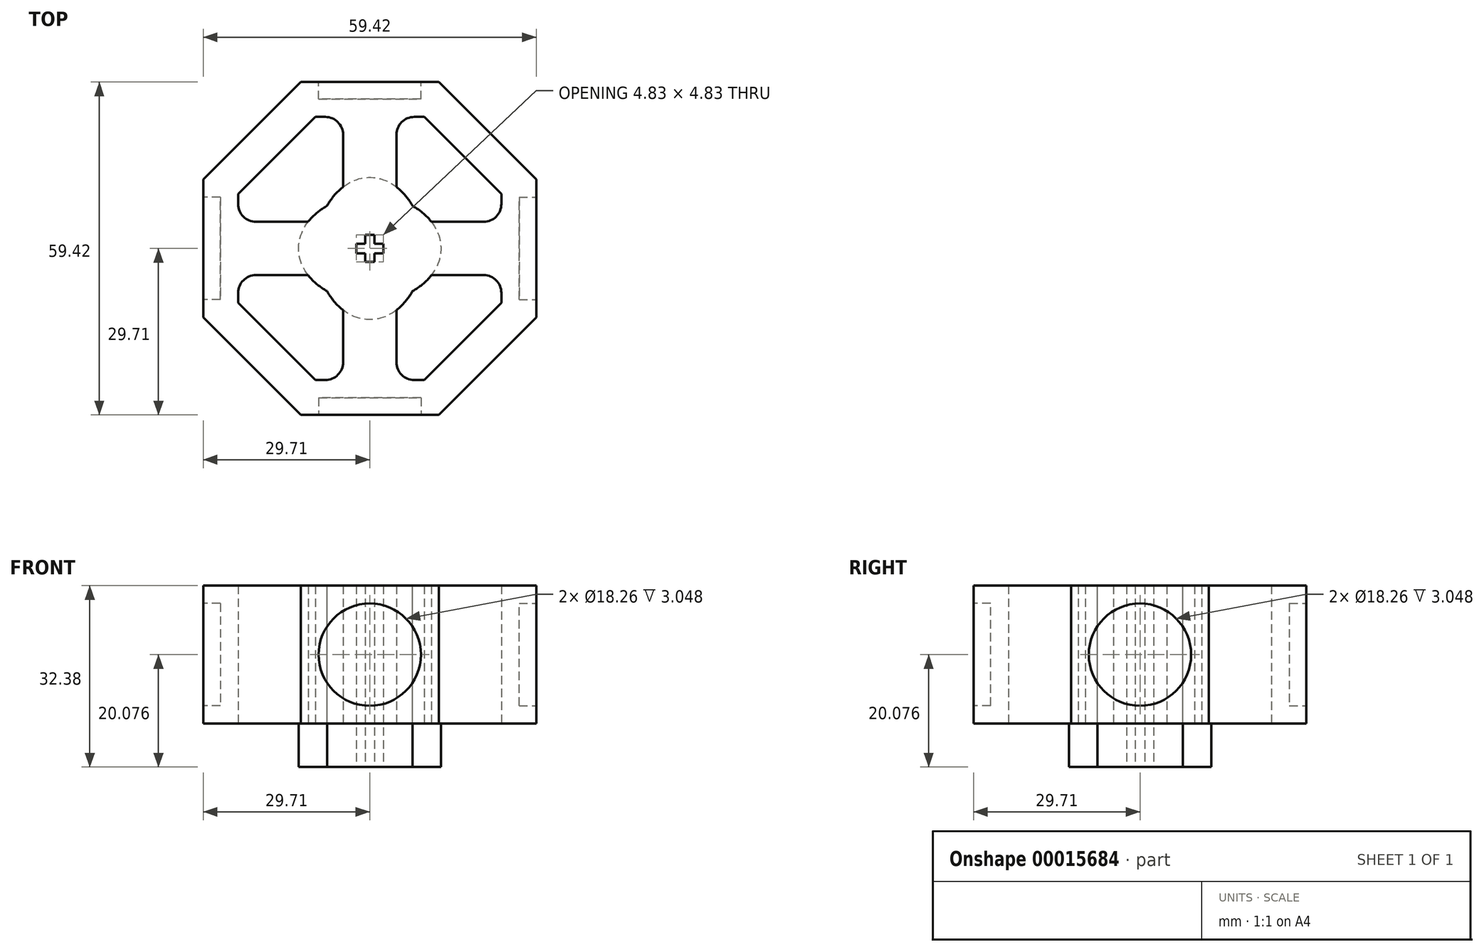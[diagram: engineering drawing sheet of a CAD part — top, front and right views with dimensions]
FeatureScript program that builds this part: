
annotation { "Feature Type Name" : "Feature", "Feature Type Description" : "" }
export const myFeature = defineFeature(function(context is Context, id is Id, definition is map)
    precondition{}
    {
        {
            var Q0;
            Q0=qCreatedBy(makeId("Top.planeOp"),FACE);
            var sketch = newSketch(context, id + "F0", { "sketchPlane" : qUnion([Q0])});
            skCircle(sketch, "E0.cCircle", {"center": v(0, 0) * mm, "radius": 29.71 * mm, "construction": true});
            skLineSegment(sketch, "E0.0", {"start": v(-12.3, 29.71) * mm, "end": v(12.3, 29.71) * mm});
            skLineSegment(sketch, "E0.1", {"start": v(12.3, 29.71) * mm, "end": v(29.71, 12.3) * mm});
            skLineSegment(sketch, "E0.2", {"start": v(29.71, 12.3) * mm, "end": v(29.71, -12.3) * mm});
            skLineSegment(sketch, "E0.3", {"start": v(29.71, -12.3) * mm, "end": v(12.3, -29.71) * mm});
            skLineSegment(sketch, "E0.4", {"start": v(12.3, -29.71) * mm, "end": v(-12.3, -29.71) * mm});
            skLineSegment(sketch, "E0.5", {"start": v(-12.3, -29.71) * mm, "end": v(-29.71, -12.3) * mm});
            skLineSegment(sketch, "E0.6", {"start": v(-29.71, -12.3) * mm, "end": v(-29.71, 12.3) * mm});
            skLineSegment(sketch, "E0.7", {"start": v(-29.71, 12.3) * mm, "end": v(-12.3, 29.71) * mm});
            skPoint(sketch, "E0.0.midPoint", {"position": v(0, 29.71) * mm});
            skLineSegment(sketch, "E1.rect.bottom", {"start": v(0.84, -2.41) * mm, "end": v(-0.84, -2.41) * mm});
            skLineSegment(sketch, "E1.rect.top", {"start": v(0.84, 2.41) * mm, "end": v(-0.84, 2.41) * mm});
            skLineSegment(sketch, "E1.rect.left", {"start": v(0.84, -2.41) * mm, "end": v(0.84, 2.41) * mm});
            skLineSegment(sketch, "E1.rect.right", {"start": v(-0.84, -2.41) * mm, "end": v(-0.84, 2.41) * mm});
            skLineSegment(sketch, "E2.rect.bottom", {"start": v(2.41, -0.84) * mm, "end": v(-2.41, -0.84) * mm});
            skLineSegment(sketch, "E2.rect.top", {"start": v(2.41, 0.84) * mm, "end": v(-2.41, 0.84) * mm});
            skLineSegment(sketch, "E2.rect.left", {"start": v(2.41, -0.84) * mm, "end": v(2.41, 0.84) * mm});
            skLineSegment(sketch, "E2.rect.right", {"start": v(-2.41, -0.84) * mm, "end": v(-2.41, 0.84) * mm});
            skSolve(sketch);
        }
        {
            var Q0;
            Q0 = qSketchRegion(id + "F0", true);
            extrude(context, id + "F1", {"entities" : qUnion([Q0]), "depth" : 24.6 * mm});
        }
        {
            var Q0;
            Q0=makeQuery(id+"F1.opExtrude","SWEPT_FACE",FACE,{"disambiguationData":[OSD([sQuery(id+"F0.wireOp",EDGE,"E0.4")])]});
            var sketch = newSketch(context, id + "F2", { "sketchPlane" : qUnion([Q0])});
            skLineSegment(sketch, "E3", {"start": v(0, 24.61) * mm, "end": v(0, 21.44) * mm});
            skLineSegment(sketch, "E4", {"start": v(0, 21.44) * mm, "end": v(0, 3.18) * mm});
            skLineSegment(sketch, "E5", {"start": v(0, 3.18) * mm, "end": v(0, 0) * mm});
            skCircle(sketch, "E6", {"center": v(0, 12.3) * mm, "radius": 9.13 * mm});
            skSolve(sketch);
        }
        {
            var Q0;
            Q0 = qSketchRegion(id + "F2", true);
            extrude(context, id + "F3", {"entities" : qUnion([Q0]), "operationType" : NewBodyOperationType.REMOVE, "oppositeDirection" : true, "depth" : 3.05 * mm});
        }
        {
            var Q0;
            Q0=makeQuery(id+"F1.opExtrude","SWEPT_FACE",FACE,{"disambiguationData":[OSD([sQuery(id+"F0.wireOp",EDGE,"E0.0")])]});
            var sketch = newSketch(context, id + "F4", { "sketchPlane" : qUnion([Q0])});
            skCircle(sketch, "E7", {"center": v(0, 12.3) * mm, "radius": 9.13 * mm});
            skSolve(sketch);
        }
        {
            var Q0;
            Q0 = qSketchRegion(id + "F4", true);
            extrude(context, id + "F5", {"entities" : qUnion([Q0]), "operationType" : NewBodyOperationType.REMOVE, "oppositeDirection" : true, "depth" : 3.05 * mm});
        }
        {
            var Q0;
            Q0=makeQuery(id+"F1.opExtrude","SWEPT_FACE",FACE,{"disambiguationData":[OSD([sQuery(id+"F0.wireOp",EDGE,"E0.6")])]});
            var sketch = newSketch(context, id + "F6", { "sketchPlane" : qUnion([Q0])});
            skLineSegment(sketch, "E8", {"start": v(0, 0) * mm, "end": v(0, 3.18) * mm});
            skLineSegment(sketch, "E9", {"start": v(0, 3.18) * mm, "end": v(0, 21.44) * mm});
            skLineSegment(sketch, "E10", {"start": v(0, 21.44) * mm, "end": v(0, 24.61) * mm});
            skCircle(sketch, "E11", {"center": v(0, 12.3) * mm, "radius": 9.13 * mm});
            skSolve(sketch);
        }
        {
            var Q0;
            Q0 = qSketchRegion(id + "F6", true);
            extrude(context, id + "F7", {"entities" : qUnion([Q0]), "operationType" : NewBodyOperationType.REMOVE, "oppositeDirection" : true, "depth" : 3.05 * mm});
        }
        {
            var Q0;
            Q0=makeQuery(id+"F1.opExtrude","SWEPT_FACE",FACE,{"disambiguationData":[OSD([sQuery(id+"F0.wireOp",EDGE,"E0.2")])]});
            var sketch = newSketch(context, id + "F8", { "sketchPlane" : qUnion([Q0])});
            skCircle(sketch, "E12", {"center": v(0, 12.3) * mm, "radius": 9.13 * mm});
            skSolve(sketch);
        }
        {
            var Q0;
            Q0 = qSketchRegion(id + "F8", true);
            extrude(context, id + "F9", {"entities" : qUnion([Q0]), "operationType" : NewBodyOperationType.REMOVE, "oppositeDirection" : true, "depth" : 3.05 * mm});
        }
        {
            var Q0;
            Q0=makeQuery(id+"F1.opExtrude","CAP_FACE",FACE,{"disambiguationData":[OSD([sQuery(id+"F0.wireOp",EDGE,"E0.0"),sQuery(id+"F0.wireOp",EDGE,"E0.1"),sQuery(id+"F0.wireOp",EDGE,"E0.2"),sQuery(id+"F0.wireOp",EDGE,"E0.3"),sQuery(id+"F0.wireOp",EDGE,"E0.4"),sQuery(id+"F0.wireOp",EDGE,"E0.5"),sQuery(id+"F0.wireOp",EDGE,"E0.6"),sQuery(id+"F0.wireOp",EDGE,"E0.7"),sQuery(id+"F0.wireOp",EDGE,"E1.rect.bottom"),sQuery(id+"F0.wireOp",EDGE,"E1.rect.top"),sQuery(id+"F0.wireOp",EDGE,"E1.rect.left"),sQuery(id+"F0.wireOp",EDGE,"E1.rect.right"),sQuery(id+"F0.wireOp",EDGE,"E2.rect.bottom"),sQuery(id+"F0.wireOp",EDGE,"E2.rect.top"),sQuery(id+"F0.wireOp",EDGE,"E2.rect.left"),sQuery(id+"F0.wireOp",EDGE,"E2.rect.right")])],"isStart":true});
            var sketch = newSketch(context, id + "F10", { "sketchPlane" : qUnion([Q0])});
            skEllipse(sketch, "E13", {"center": v(0, 0) * mm, "majorRadius": 12.7 * mm, "minorRadius": 9.53 * mm, "majorAxis": v(0, 1)});
            skEllipse(sketch, "E14", {"center": v(0, 0) * mm, "majorRadius": 12.7 * mm, "minorRadius": 9.53 * mm, "majorAxis": v(1, 0)});
            skSolve(sketch);
        }
        {
            var Q0;
            {var subQ0=sQuery(id+"F10.wireOp",EDGE,"E14");var subQ1=sQuery(id+"F10.wireOp",EDGE,"E13");var subQ3=makeQuery(id+"F10.imprint","INTERSECT",VERTEX,{"disambiguationData":[OD(0.0)],"derivedFrom":[subQ1,subQ0]});Q0=makeQuery(id+"F10.imprint","IMPRINT",FACE,{"disambiguationData":[TD([[makeQuery(id+"F10.imprint","IMPRINT",EDGE,{"disambiguationData":[TD([[subQ3,1.0]])],"derivedFrom":subQ1}),-1.0]])]});}
            var Q1;
            {var subQ0=sQuery(id+"F10.wireOp",EDGE,"E14");var subQ1=sQuery(id+"F10.wireOp",EDGE,"E13");var subQ3=makeQuery(id+"F10.imprint","INTERSECT",VERTEX,{"disambiguationData":[OD(0.0)],"derivedFrom":[subQ1,subQ0]});Q1=makeQuery(id+"F10.imprint","IMPRINT",FACE,{"disambiguationData":[TD([[makeQuery(id+"F10.imprint","IMPRINT",EDGE,{"disambiguationData":[TD([[subQ3,-1.0]])],"derivedFrom":subQ1}),1.0]])]});}
            var Q2;
            {var subQ0=sQuery(id+"F10.wireOp",EDGE,"E14");var subQ1=sQuery(id+"F10.wireOp",EDGE,"E13");var subQ3=makeQuery(id+"F10.imprint","INTERSECT",VERTEX,{"disambiguationData":[OD(2.0)],"derivedFrom":[subQ1,subQ0]});Q2=makeQuery(id+"F10.imprint","IMPRINT",FACE,{"disambiguationData":[TD([[makeQuery(id+"F10.imprint","IMPRINT",EDGE,{"disambiguationData":[TD([[subQ3,-1.0]])],"derivedFrom":subQ1}),-1.0]])]});}
            var Q3;
            {var subQ0=sQuery(id+"F10.wireOp",EDGE,"E14");var subQ1=sQuery(id+"F10.wireOp",EDGE,"E13");var subQ3=makeQuery(id+"F10.imprint","INTERSECT",VERTEX,{"disambiguationData":[OD(1.0)],"derivedFrom":[subQ1,subQ0]});Q3=makeQuery(id+"F10.imprint","IMPRINT",FACE,{"disambiguationData":[TD([[makeQuery(id+"F10.imprint","IMPRINT",EDGE,{"disambiguationData":[TD([[subQ3,1.0]])],"derivedFrom":subQ1}),1.0]])]});}
            var Q4;
            {var subQ10=sQuery(id+"F0.wireOp",EDGE,"E1.rect.bottom");Q4=makeQuery(id+"F10.imprint","IMPRINT",FACE,{"disambiguationData":[TD([[makeQuery(id+"F10.imprint","IMPRINT",EDGE,{"derivedFrom":makeQuery(id+"F1.opExtrude","CAP_EDGE",EDGE,{"disambiguationData":[OSD([subQ10])],"isStart":true})}),-1.0]])]});}
            extrude(context, id + "F11", {"entities" : qUnion([Q0, Q1, Q2, Q3, Q4]), "operationType" : NewBodyOperationType.ADD, "depth" : 7.77 * mm});
        }
        {
            var Q0;
            Q0=makeQuery(id+"F1.opExtrude","CAP_FACE",FACE,{"disambiguationData":[OSD([sQuery(id+"F0.wireOp",EDGE,"E0.0"),sQuery(id+"F0.wireOp",EDGE,"E0.1"),sQuery(id+"F0.wireOp",EDGE,"E0.2"),sQuery(id+"F0.wireOp",EDGE,"E0.3"),sQuery(id+"F0.wireOp",EDGE,"E0.4"),sQuery(id+"F0.wireOp",EDGE,"E0.5"),sQuery(id+"F0.wireOp",EDGE,"E0.6"),sQuery(id+"F0.wireOp",EDGE,"E0.7"),sQuery(id+"F0.wireOp",EDGE,"E1.rect.bottom"),sQuery(id+"F0.wireOp",EDGE,"E1.rect.top"),sQuery(id+"F0.wireOp",EDGE,"E1.rect.left"),sQuery(id+"F0.wireOp",EDGE,"E1.rect.right"),sQuery(id+"F0.wireOp",EDGE,"E2.rect.bottom"),sQuery(id+"F0.wireOp",EDGE,"E2.rect.top"),sQuery(id+"F0.wireOp",EDGE,"E2.rect.left"),sQuery(id+"F0.wireOp",EDGE,"E2.rect.right")])],"isStart":true});
            var sketch = newSketch(context, id + "F12", { "sketchPlane" : qUnion([Q0])});
            skCircle(sketch, "E15.cCircle", {"center": v(0, 0) * mm, "radius": 23.49 * mm, "construction": true});
            skLineSegment(sketch, "E15.0", {"start": v(23.49, -9.73) * mm, "end": v(9.73, -23.49) * mm});
            skLineSegment(sketch, "E15.1", {"start": v(9.73, -23.49) * mm, "end": v(-9.73, -23.49) * mm});
            skLineSegment(sketch, "E15.2", {"start": v(-9.73, -23.49) * mm, "end": v(-23.49, -9.73) * mm});
            skLineSegment(sketch, "E15.3", {"start": v(-23.49, -9.73) * mm, "end": v(-23.49, 9.73) * mm});
            skLineSegment(sketch, "E15.4", {"start": v(-23.49, 9.73) * mm, "end": v(-9.73, 23.49) * mm});
            skLineSegment(sketch, "E15.5", {"start": v(-9.73, 23.49) * mm, "end": v(9.73, 23.49) * mm});
            skLineSegment(sketch, "E15.6", {"start": v(9.73, 23.49) * mm, "end": v(23.49, 9.73) * mm});
            skLineSegment(sketch, "E15.7", {"start": v(23.49, 9.73) * mm, "end": v(23.49, -9.73) * mm});
            skPoint(sketch, "E15.0.midPoint", {"position": v(16.6, -16.6) * mm});
            skEllipse(sketch, "E16", {"center": v(0, 0) * mm, "majorRadius": 12.7 * mm, "minorRadius": 9.53 * mm, "majorAxis": v(1, 0)});
            skEllipse(sketch, "E17", {"center": v(0, 0) * mm, "majorRadius": 12.7 * mm, "minorRadius": 9.53 * mm, "majorAxis": v(0, -1)});
            skLineSegment(sketch, "E18", {"start": v(16.6, -16.6) * mm, "end": v(21, -21) * mm});
            skLineSegment(sketch, "E19.bottom", {"start": v(-4.76, -11) * mm, "end": v(4.76, -11) * mm});
            skLineSegment(sketch, "E19.top", {"start": v(-4.76, -23.49) * mm, "end": v(4.76, -23.49) * mm});
            skLineSegment(sketch, "E19.left", {"start": v(-4.76, -11) * mm, "end": v(-4.76, -23.49) * mm});
            skLineSegment(sketch, "E19.right", {"start": v(4.76, -11) * mm, "end": v(4.76, -23.49) * mm});
            skLineSegment(sketch, "E20.bottom", {"start": v(-11, -4.76) * mm, "end": v(-23.49, -4.76) * mm});
            skLineSegment(sketch, "E20.top", {"start": v(-11, 4.76) * mm, "end": v(-23.49, 4.76) * mm});
            skLineSegment(sketch, "E20.left", {"start": v(-11, -4.76) * mm, "end": v(-11, 4.76) * mm});
            skLineSegment(sketch, "E20.right", {"start": v(-23.49, -4.76) * mm, "end": v(-23.49, 4.76) * mm});
            skLineSegment(sketch, "E21.bottom", {"start": v(4.76, 11) * mm, "end": v(-4.76, 11) * mm});
            skLineSegment(sketch, "E21.top", {"start": v(4.76, 23.49) * mm, "end": v(-4.76, 23.49) * mm});
            skLineSegment(sketch, "E21.left", {"start": v(4.76, 11) * mm, "end": v(4.76, 23.49) * mm});
            skLineSegment(sketch, "E21.right", {"start": v(-4.76, 11) * mm, "end": v(-4.76, 23.49) * mm});
            skPoint(sketch, "E22", {"position": v(-23.49, 0) * mm});
            skPoint(sketch, "E23", {"position": v(0, -23.49) * mm});
            skPoint(sketch, "E24", {"position": v(0, 23.49) * mm});
            skLineSegment(sketch, "E25.bottom", {"start": v(11, 4.76) * mm, "end": v(23.49, 4.76) * mm});
            skLineSegment(sketch, "E25.top", {"start": v(11, -4.76) * mm, "end": v(23.49, -4.76) * mm});
            skLineSegment(sketch, "E25.left", {"start": v(11, 4.76) * mm, "end": v(11, -4.76) * mm});
            skLineSegment(sketch, "E25.right", {"start": v(23.49, 4.76) * mm, "end": v(23.49, -4.76) * mm});
            skSolve(sketch);
        }
        {
            var Q0;
            {var subQ2=sQuery(id+"F12.wireOp",EDGE,"E19.right");Q0=makeQuery(id+"F12.imprint","IMPRINT",FACE,{"disambiguationData":[TD([[makeQuery(id+"F12.imprint","IMPRINT",EDGE,{"derivedFrom":subQ2}),1.0]])]});}
            var Q1;
            {var subQ6=sQuery(id+"F12.wireOp",EDGE,"E15.2");Q1=makeQuery(id+"F12.imprint","IMPRINT",FACE,{"disambiguationData":[TD([[makeQuery(id+"F12.imprint","IMPRINT",EDGE,{"derivedFrom":subQ6}),-1.0]])]});}
            var Q2;
            {var subQ6=sQuery(id+"F12.wireOp",EDGE,"E15.4");Q2=makeQuery(id+"F12.imprint","IMPRINT",FACE,{"disambiguationData":[TD([[makeQuery(id+"F12.imprint","IMPRINT",EDGE,{"derivedFrom":subQ6}),-1.0]])]});}
            var Q3;
            {var subQ6=sQuery(id+"F12.wireOp",EDGE,"E15.6");Q3=makeQuery(id+"F12.imprint","IMPRINT",FACE,{"disambiguationData":[TD([[makeQuery(id+"F12.imprint","IMPRINT",EDGE,{"derivedFrom":subQ6}),-1.0]])]});}
            var Q4;
            Q4=makeQuery(id+"F1.opExtrude","CAP_FACE",FACE,{"disambiguationData":[OSD([sQuery(id+"F0.wireOp",EDGE,"E0.0"),sQuery(id+"F0.wireOp",EDGE,"E0.1"),sQuery(id+"F0.wireOp",EDGE,"E0.2"),sQuery(id+"F0.wireOp",EDGE,"E0.3"),sQuery(id+"F0.wireOp",EDGE,"E0.4"),sQuery(id+"F0.wireOp",EDGE,"E0.5"),sQuery(id+"F0.wireOp",EDGE,"E0.6"),sQuery(id+"F0.wireOp",EDGE,"E0.7"),sQuery(id+"F0.wireOp",EDGE,"E1.rect.bottom"),sQuery(id+"F0.wireOp",EDGE,"E1.rect.top"),sQuery(id+"F0.wireOp",EDGE,"E1.rect.left"),sQuery(id+"F0.wireOp",EDGE,"E1.rect.right"),sQuery(id+"F0.wireOp",EDGE,"E2.rect.bottom"),sQuery(id+"F0.wireOp",EDGE,"E2.rect.top"),sQuery(id+"F0.wireOp",EDGE,"E2.rect.left"),sQuery(id+"F0.wireOp",EDGE,"E2.rect.right")])],"isStart":false});
            extrude(context, id + "F13", {"entities" : qUnion([Q0, Q1, Q2, Q3]), "operationType" : NewBodyOperationType.REMOVE, "endBound" : BoundingType.UP_TO_SURFACE, "oppositeDirection" : true, "endBoundEntityFace" : qUnion([Q4]), "depth" : 25.4 * mm});
        }
        {
            var Q0;
            Q0=makeQuery(id+"F13.boolean.opBoolean","COPY",EDGE,{"derivedFrom":makeQuery(id+"F13.opExtrude","SWEPT_EDGE",EDGE,{"disambiguationData":[OSD([sQuery(id+"F12.wireOp",EDGE,"E15.7"),sQuery(id+"F12.wireOp",EDGE,"E25.top"),sQuery(id+"F12.wireOp",EDGE,"E25.right")])]})});
            var Q1;
            Q1=makeQuery(id+"F13.boolean.opBoolean","COPY",EDGE,{"derivedFrom":makeQuery(id+"F13.opExtrude","SWEPT_EDGE",EDGE,{"disambiguationData":[OSD([sQuery(id+"F12.wireOp",EDGE,"E15.7"),sQuery(id+"F12.wireOp",EDGE,"E25.bottom"),sQuery(id+"F12.wireOp",EDGE,"E25.right")])]})});
            var Q2;
            Q2=makeQuery(id+"F13.boolean.opBoolean","COPY",EDGE,{"derivedFrom":makeQuery(id+"F13.opExtrude","SWEPT_EDGE",EDGE,{"disambiguationData":[OSD([sQuery(id+"F12.wireOp",EDGE,"E15.3"),sQuery(id+"F12.wireOp",EDGE,"E20.top"),sQuery(id+"F12.wireOp",EDGE,"E20.right")])]})});
            var Q3;
            Q3=makeQuery(id+"F13.boolean.opBoolean","COPY",EDGE,{"derivedFrom":makeQuery(id+"F13.opExtrude","SWEPT_EDGE",EDGE,{"disambiguationData":[OSD([sQuery(id+"F12.wireOp",EDGE,"E15.5"),sQuery(id+"F12.wireOp",EDGE,"E21.top"),sQuery(id+"F12.wireOp",EDGE,"E21.right")])]})});
            var Q4;
            Q4=makeQuery(id+"F13.boolean.opBoolean","COPY",EDGE,{"derivedFrom":makeQuery(id+"F13.opExtrude","SWEPT_EDGE",EDGE,{"disambiguationData":[OSD([sQuery(id+"F12.wireOp",EDGE,"E15.5"),sQuery(id+"F12.wireOp",EDGE,"E21.top"),sQuery(id+"F12.wireOp",EDGE,"E21.left")])]})});
            var Q5;
            Q5=makeQuery(id+"F13.boolean.opBoolean","COPY",EDGE,{"derivedFrom":makeQuery(id+"F13.opExtrude","SWEPT_EDGE",EDGE,{"disambiguationData":[OSD([sQuery(id+"F12.wireOp",EDGE,"E15.1"),sQuery(id+"F12.wireOp",EDGE,"E19.top"),sQuery(id+"F12.wireOp",EDGE,"E19.right")])]})});
            var Q6;
            Q6=makeQuery(id+"F13.boolean.opBoolean","COPY",EDGE,{"derivedFrom":makeQuery(id+"F13.opExtrude","SWEPT_EDGE",EDGE,{"disambiguationData":[OSD([sQuery(id+"F12.wireOp",EDGE,"E15.1"),sQuery(id+"F12.wireOp",EDGE,"E19.top"),sQuery(id+"F12.wireOp",EDGE,"E19.left")])]})});
            var Q7;
            Q7=makeQuery(id+"F13.boolean.opBoolean","COPY",EDGE,{"derivedFrom":makeQuery(id+"F13.opExtrude","SWEPT_EDGE",EDGE,{"disambiguationData":[OSD([sQuery(id+"F12.wireOp",EDGE,"E15.3"),sQuery(id+"F12.wireOp",EDGE,"E20.bottom"),sQuery(id+"F12.wireOp",EDGE,"E20.right")])]})});
            fillet(context, id + "F14", {"entities" : qUnion([Q0, Q1, Q2, Q3, Q4, Q5, Q6, Q7]), "radius" : 3.17 * mm, "tangentPropagation" : true, "allowEdgeOverflow" : false});
        }
    });
